# Revit family: Innovo GB_IR 20 200 GB NAT
name_source: partatom
category: Mechanical Equipment
revit_build: Autodesk Revit 2015 (Build: 20160512_0715(x64)
units: mm (PartAtom-declared; Revit-internal decimal feet)

## types (1)
- IR-20-200 GB NAT
    1e Maintenance (check-up) = 3 months after installation
    2nd Maintenance (general maintenance) = 12 months after installation
    APS Pressure < = 115.0 Pa
    Annual electricity consumption (1) = 40 kWh
    Annual electricity consumption (2) = 42 kWh
    Annual fuel consumption (1) = 16 GJ GCV
    Annual fuel consumption (2) = 21 GJ GCV
    Assembly Code = D3010
    BIM Content Developer = CAD & Company
    CE-PIN = 0063CQ3037
    Co2 Emissions (tol. +/- 1.0) vol% = 9.3
    Cold Water Connection R = 3/4"
    Condens Discharge Connection = 40 mm  [stored 0.131234 ft]
    Default Setpoint = 65 °C
    Description = Condensing High Efficiency Storage Water Heater
    Destination / Country = UK & Ireland
    Diameter = 560 mm  [stored 1.83727 ft]
    Drain Valve Connection Rp = 3/4"
    Draw-off Capacity @ ΔT = 28°C after 120 min. = 1600.0 L
    Draw-off Capacity @ ΔT = 28°C after 30 min. = 700.0 L
    Draw-off Capacity @ ΔT = 28°C after 60 min. = 990.0 L
    Draw-off Capacity @ ΔT = 28°C after 90 min. = 1300.0 L
    Draw-off Capacity @ ΔT = 44°C after 120 min. = 990.0 L
    Draw-off Capacity @ ΔT = 44°C after 30 min. = 430.0 L
    Draw-off Capacity @ ΔT = 44°C after 60 min. = 620.0 L
    Draw-off Capacity @ ΔT = 44°C after 90 min. = 810.0 L
    Draw-off Capacity @ ΔT = 50°C after 120 min. = 870.0 L
    Draw-off Capacity @ ΔT = 50°C after 30 min. = 380.0 L
    Draw-off Capacity @ ΔT = 50°C after 60 min. = 540.0 L
    Draw-off Capacity @ ΔT = 50°C after 90 min. = 710.0 L
    Draw-off Capacity @ ΔT = 55°C after 120 min. = 790.0 L
    Draw-off Capacity @ ΔT = 55°C after 30 min. = 340.0 L
    Draw-off Capacity @ ΔT = 55°C after 60 min. = 490.0 L
    Draw-off Capacity @ ΔT = 55°C after 90 min. = 640.0 L
    Draw-off Capacity @ ΔT = 70°C after 120 min. = 610.0 L
    Draw-off Capacity @ ΔT = 70°C after 30 min. = 250.0 L
    Draw-off Capacity @ ΔT = 70°C after 60 min. = 370.0 L
    Draw-off Capacity @ ΔT = 70°C after 90 min. = 490.0 L
    Empty Weight = 106 kg
    Energy Efficiency Rating (Hi, acc NEN-EN 89-1999) = 106
    Energy Efficiency Rating (Hs, acc NEN-EN 89-1999) = 95
    Flue Diameter - concentric system = 80/125 mm/mm
    Flue Diameter - parallel system = 2x80
    Flue Diameter - water heater = 80/125 mm/mm
    Frequency = 50 Hz
    Gas Category = II2E3P
    Gas Connection R = 15"
    Gas Flow Rate - Mass kg/h = n.a.
    Gas Flow Rate - Volume ltr/hr = 1.9
    Gas Supply Pressure = 2000.0 Pa
    Heating Up Time @ ΔT = 28°C = 17
    Heating Up Time @ ΔT = 44°C = 27
    Heating Up Time @ ΔT = 50°C = 30
    Heating Up Time @ ΔT = 55°C = 33
    Heating Up Time @ ΔT = 70°C = 42
    Height = 1545 mm
    Height Air Inlet = 1305 mm
    Height Cold Water Inlet = 170 mm  [stored 0.557743 ft]
    Height Flue Outlet = 1305 mm
    Height Gas Connection = 860 mm
    Height Warm Water Outlet = 1545 mm
    Hot / Warm Water Connection R = 3/4"
    Indoor sound power level = 52 dB
    Installation Type = B23/C13/C33/C43/C53/C63
    Insulation Thickness = 50 mm  [stored 0.164042 ft]
    Length = 780 mm  [stored 2.55906 ft]
    Load profile = XL
    Maintenance Interval = 12 months
    Manufacturer = A.O. Smith Water Products Company b.v.
    Manufacturer Number = E 7110
    Max. Flue Gas Outlet Temperature = 61 °C
    Max. Operating Pressure = 800000.0 Pa
    Max. Setpoint = 85 °C
    Min. Setpoint = 40 °C
    Model = IR-20-200 GB NAT
    Model identifier = IR-20-200
    NOx Emissions (air free, 0% O2) ppm = 19
    NOx Emissions mg/kWh = 30
    Noice-level dB (A) = <45
    Nominal Heat Input (Gross) = 20000
    Nominal Heat Input (Net) = 18000
    Nominal Output = 19100
    Operating Weight = 332 kg
    Other load profile = XXL
    Packaging Height = 1695 mm
    Packaging Length = 946 mm
    Packaging Width = 786 mm
    Phase = 1
    Power Consumption (nominal) = 36 W
    Power Consumption (peak) = 85 W
    Precaustions during assembling, installation or maintenance = see User, Installation, Service and Maintenance Manual
    Recovery Rate @ ΔT = 28°C = 590.0 L/s
    Recovery Rate @ ΔT = 44°C = 380.0 L/s
    Recovery Rate @ ΔT = 50°C = 330.0 L/s
    Recovery Rate @ ΔT = 55°C = 300.0 L/s
    Recovery Rate @ ΔT = 70°C = 240.0 L/s
    Seasonal Energy Efficiency Rating = 95
    Serial Number = 8717449286118
    Smart control = No
    Stand-by Loss = 0 W
    Stand-by Loss - daily (24h) = 0 W
    Standard Set For = G20
    Storage Capacity = 200.0 L
    T&P Connection Rp = 3/4"
    Thermostat temperature setting = 65 °C
    Trade mark = A.O. Smith
    Transport Weight = 122 kg
    Type of Packaging = Carton and Wood
    URL = www.aosmith.co.uk
    Valve Height 01 = 604 mm  [stored 1.98163 ft]
    Valve Height 02 = 1328 mm  [stored 4.35696 ft]
    Voltage = 230 V
    Warranty on parts = 12 months
    Warranty on tank = 36 months
    Water heating energy efficiency (1) = 91%
    Water heating energy efficiency (2) = 90%
    Water heating energy efficiency class (1) = A
    Water heating energy efficiency class (2) = A
    Width = 560 mm  [stored 1.83727 ft]
    Working only during off-peak hour = No
    Workspace Front Distance = 1000 mm  [stored 3.28084 ft]
    Workspace Height = 2545 mm
    Workspace Radius = 730 mm  [stored 2.39501 ft]

note: [stored X ft] marks values corroborated as IEEE doubles in the binary element streams (Revit-internal decimal feet)

## geometry (parser evidence)
native form markers: Blend x26, Sweep x26
no freeform markers — native parametric forms only
